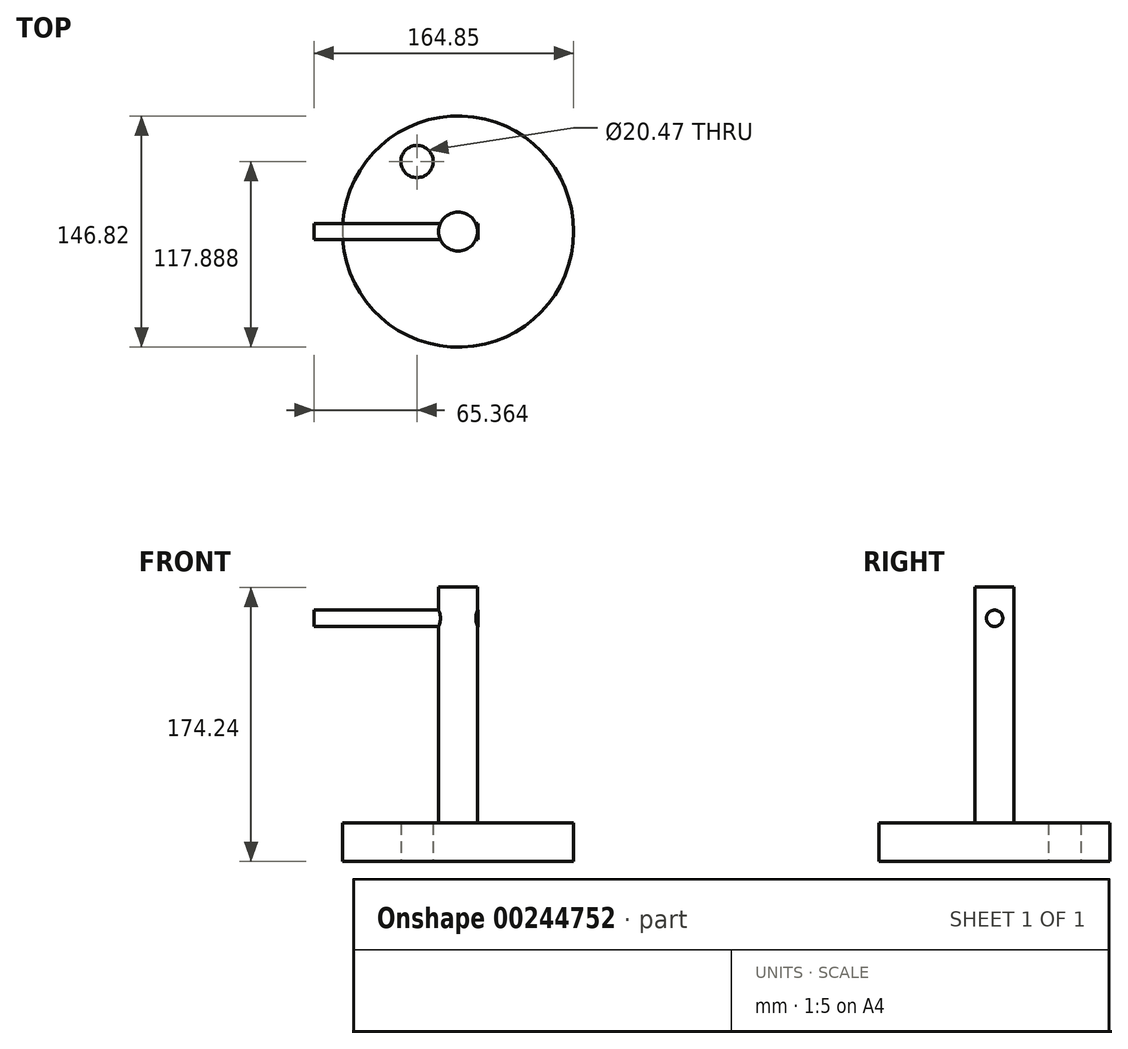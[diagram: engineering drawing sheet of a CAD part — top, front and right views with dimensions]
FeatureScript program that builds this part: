
annotation { "Feature Type Name" : "Feature", "Feature Type Description" : "" }
export const myFeature = defineFeature(function(context is Context, id is Id, definition is map)
    precondition{}
    {
        {
            var Q0;
            Q0=qCreatedBy(makeId("Top.planeOp"),FACE);
            var sketch = newSketch(context, id + "F0", { "sketchPlane" : qUnion([Q0])});
            skCircle(sketch, "E0", {"center": v(0, 0) * mm, "radius": 12.38 * mm});
            skSolve(sketch);
        }
        {
            var Q0;
            Q0 = qSketchRegion(id + "F0", true);
            extrude(context, id + "F1", {"entities" : qUnion([Q0]), "depth" : 174.24 * mm});
        }
        {
            var Q0;
            Q0=qCreatedBy(makeId("Right.planeOp"),FACE);
            cPlane(context, id + "F2", {"entities" : qUnion([Q0]), "cplaneType" : CPlaneType.OFFSET, "offset" : 12.7 * mm, "width" : 152.4 * mm, "height" : 152.4 * mm});
        }
        {
            var Q0;
            Q0=qCreatedBy(id+"F2.planeOp",FACE);
            var sketch = newSketch(context, id + "F3", { "sketchPlane" : qUnion([Q0])});
            skCircle(sketch, "E1", {"center": v(0, 154.52) * mm, "radius": 5.2 * mm});
            skSolve(sketch);
        }
        {
            var Q0;
            Q0 = qSketchRegion(id + "F3", true);
            extrude(context, id + "F4", {"entities" : qUnion([Q0]), "operationType" : NewBodyOperationType.ADD, "oppositeDirection" : true, "depth" : 104.14 * mm});
        }
        {
            var Q0;
            Q0=qCreatedBy(makeId("Top.planeOp"),FACE);
            var sketch = newSketch(context, id + "F5", { "sketchPlane" : qUnion([Q0])});
            skCircle(sketch, "E2", {"center": v(0, 0) * mm, "radius": 73.4 * mm});
            skSolve(sketch);
        }
        {
            var Q0;
            Q0 = qSketchRegion(id + "F5", true);
            extrude(context, id + "F6", {"entities" : qUnion([Q0]), "operationType" : NewBodyOperationType.ADD, "depth" : 24.38 * mm});
        }
        {
            var Q0;
            Q0=qCreatedBy(makeId("Top.planeOp"),FACE);
            var sketch = newSketch(context, id + "F7", { "sketchPlane" : qUnion([Q0])});
            skCircle(sketch, "E3", {"center": v(-26.08, 44.48) * mm, "radius": 10.24 * mm});
            skSolve(sketch);
        }
        {
            var Q0;
            Q0=makeQuery(id+"F7.imprint","IMPRINT",FACE,{"disambiguationData":[TD([[makeQuery(id+"F7.imprint","IMPRINT",EDGE,{"derivedFrom":sQuery(id+"F7.wireOp",EDGE,"E3")}),1.0]])]});
            extrude(context, id + "F8", {"entities" : qUnion([Q0]), "operationType" : NewBodyOperationType.REMOVE, "depth" : 25.4 * mm});
        }
    });
